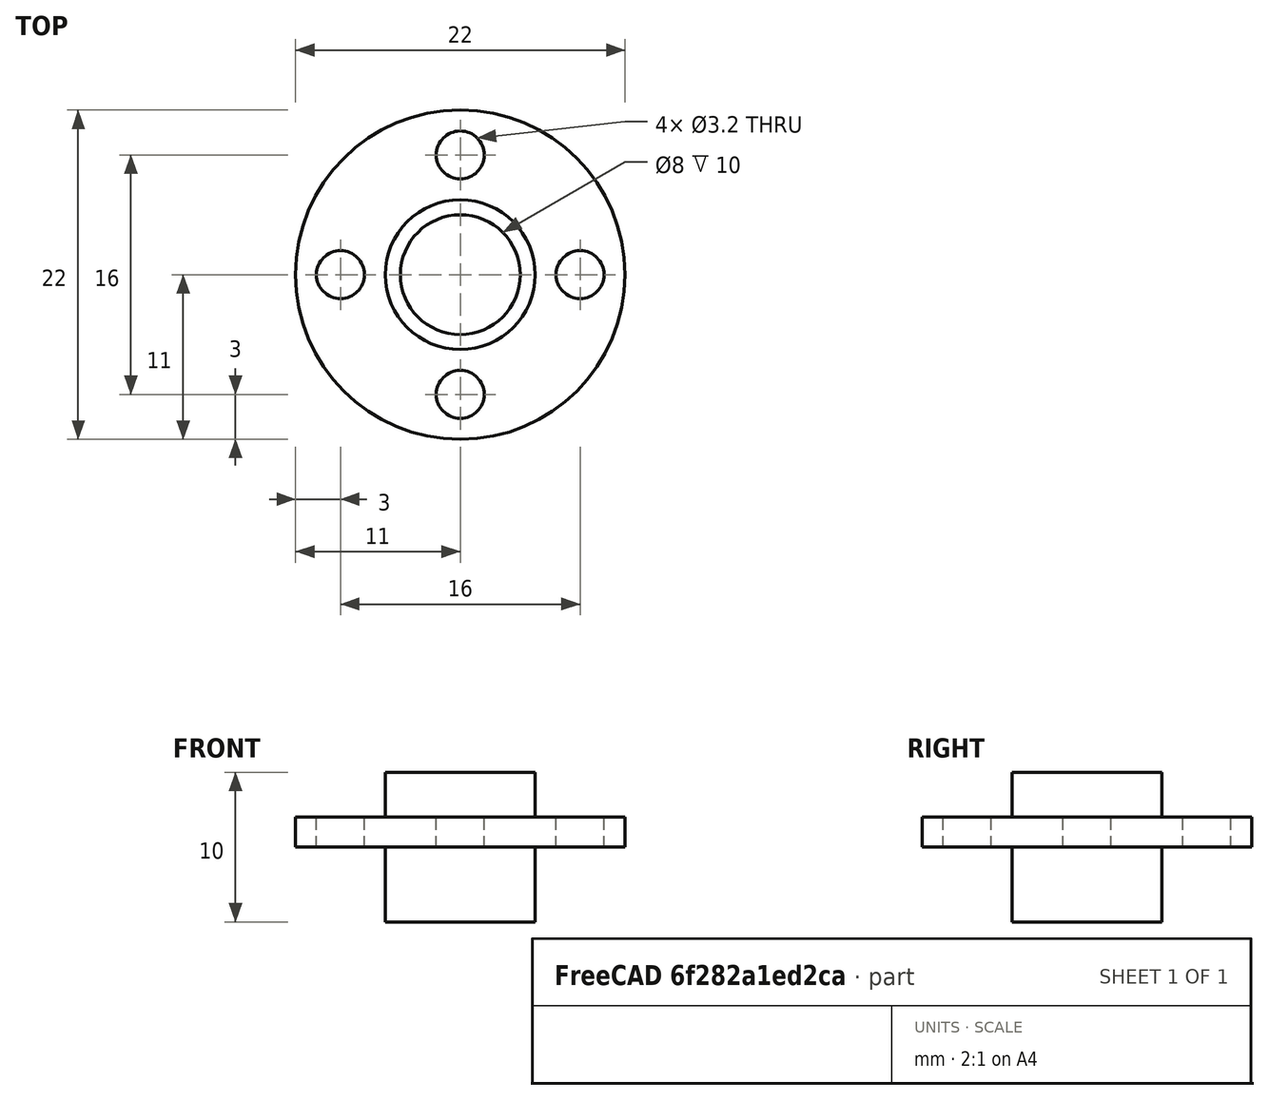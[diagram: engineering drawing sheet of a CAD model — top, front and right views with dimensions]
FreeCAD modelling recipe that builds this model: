
FCSTD DOCUMENT  (FreeCAD 0.14R3703 (Git))
Label: rosca
License: CC-BY 3.0
LicenseURL: http://creativecommons.org/licenses/by/3.0/
objects: Part::Cylinder×4, Part::Cut×2, Part::Fuse×1, Part::FeaturePython×1, Part::Feature×1
note: 9 computed .brp shape members not serialized (recipe doc carries the construction recipe); baked Part::Feature solids carry a one-line shape summary decoded from their .brp

FEATURE [Part::Cylinder] Cylinder  label="Cilindro"
  Angle = 360
  Height = 350
  Radius = 4
FEATURE [Part::Cylinder] Cylinder001  label="exterior"
  Angle = 360
  Height = 2
  Placement = pos=(0,0,5) rot=(0,0,1;0rad)
  Radius = 11
FEATURE [Part::Cylinder] Cylinder002  label="interior"
  Angle = 360
  Height = 10
  Radius = 5
FEATURE [Part::Fuse] Fusion
  Base = -> Cylinder001
  Placement = pos=(0,0,6) rot=(0,0,1;0rad)
  Tool = -> Cylinder002
FEATURE [Part::Cut] Cut  label="rosca_sin"
  Base = -> Fusion
  Tool = -> Cylinder
FEATURE [Part::Cylinder] Cylinder003  label="Cilindro001"
  Angle = 360
  Height = 23
  Placement = pos=(8,0,0) rot=(0,0,1;0rad)
  Radius = 1.6
FEATURE [Part::FeaturePython] Array  # Draft array (typed FeaturePython)
  Angle = 360
  ArrayType = 1
  Axis = (0,0,1)
  Base = -> Cylinder003
  Center = (0,0,0)
  IntervalX = (1,0,0)
  IntervalY = (0,1,0)
  IntervalZ = (0,0,1)
  NumberPolar = 4
  NumberX = 2
  NumberY = 2
  NumberZ = 1
FEATURE [Part::Cut] Cut001  label="rosca_husillo"
  Base = -> Cut
  Placement = pos=(0,0,-6) rot=(0,0,1;0rad)
  Tool = -> Array
FEATURE [Part::Feature] Cut001001  label="rosca_husillo001"
  Placement = pos=(0,0,-6) rot=(0,0,1;0rad)
  shape: bbox 22 x 22 x 10 mm, 12 faces (baked)
